# Revit family: Haworth_Planes_CollaborativeTable_Polygon
name_source: partatom
category: Furniture Systems
revit_build: Autodesk Revit 2018 (Build: 20170223_1515(x64)
units: mm (PartAtom-declared; Revit-internal decimal feet)

## family parameters
Always vertical = Yes
Cut with Voids When Loaded = No
OmniClass Number = 23.40.70.14.64.21
OmniClass Title = Systems Furniture
Part Type = Normal
Room Calculation Point = No
Round Connector Dimension = Use Diameter
Shared = No
Work Plane-Based = No

## types (2) — shared parameters
Actual Height = 29"
Assembly Code = E2020200
Caster Finish = Haworth _ Paint _ Metallic Champagne
Casters = Yes
Cutout = Yes
Cutout Depth = 4"
Cutout Width = 8"
Edgeband = Yes
Flip Top = Yes
Flip Top Depth = 4 7/16"
Flip Top Finish = Haworth _ Paint _ Metallic Champagne
Flip Top Width = 8 5/16"
Glides = No
Knife Edge = No
Leg Height = 27 13/16"
Manufacturer = Haworth
Max. Depth = 36"
Max. Width = 72"
Min. Depth = 30"
Min. Width = 60"
Min/Max Depth = 30 or 36 in.
Min/Max Width = 60 or 72 in.
Model = TACV
Opening Single = Yes
Opening Single Wide = No
Revision Number = 6
Size = Verify Final Dim. w/ Haworth
Support Spacing - From Edge = 15"
Table Thickness = 1 3/16"
URL = www.haworth.com
URL - Product = http://www.haworth.com
Warranty = http://www.haworth.com

## per-type parameters (varying)
| type | Actual Depth | Actual Width | Description | Large | Small | Stretcher Width | Sustainability Info |
| 72w 36d | 43 115/128" | 77 55/128" | Haworth - Planes Collaborative Table - Polygon - 72w 36d | Yes | No | 47 55/128" | https://www.haworth.com |
| 60w 30d | 36 143/256" | 65 115/128" | Haworth - Planes Collaborative Table - Polygon - 60w 30d | No | Yes | 35 115/128" | http://www.haworth.com |

## geometry (parser evidence)
native form markers: Sweep x15
no freeform markers — native parametric forms only
